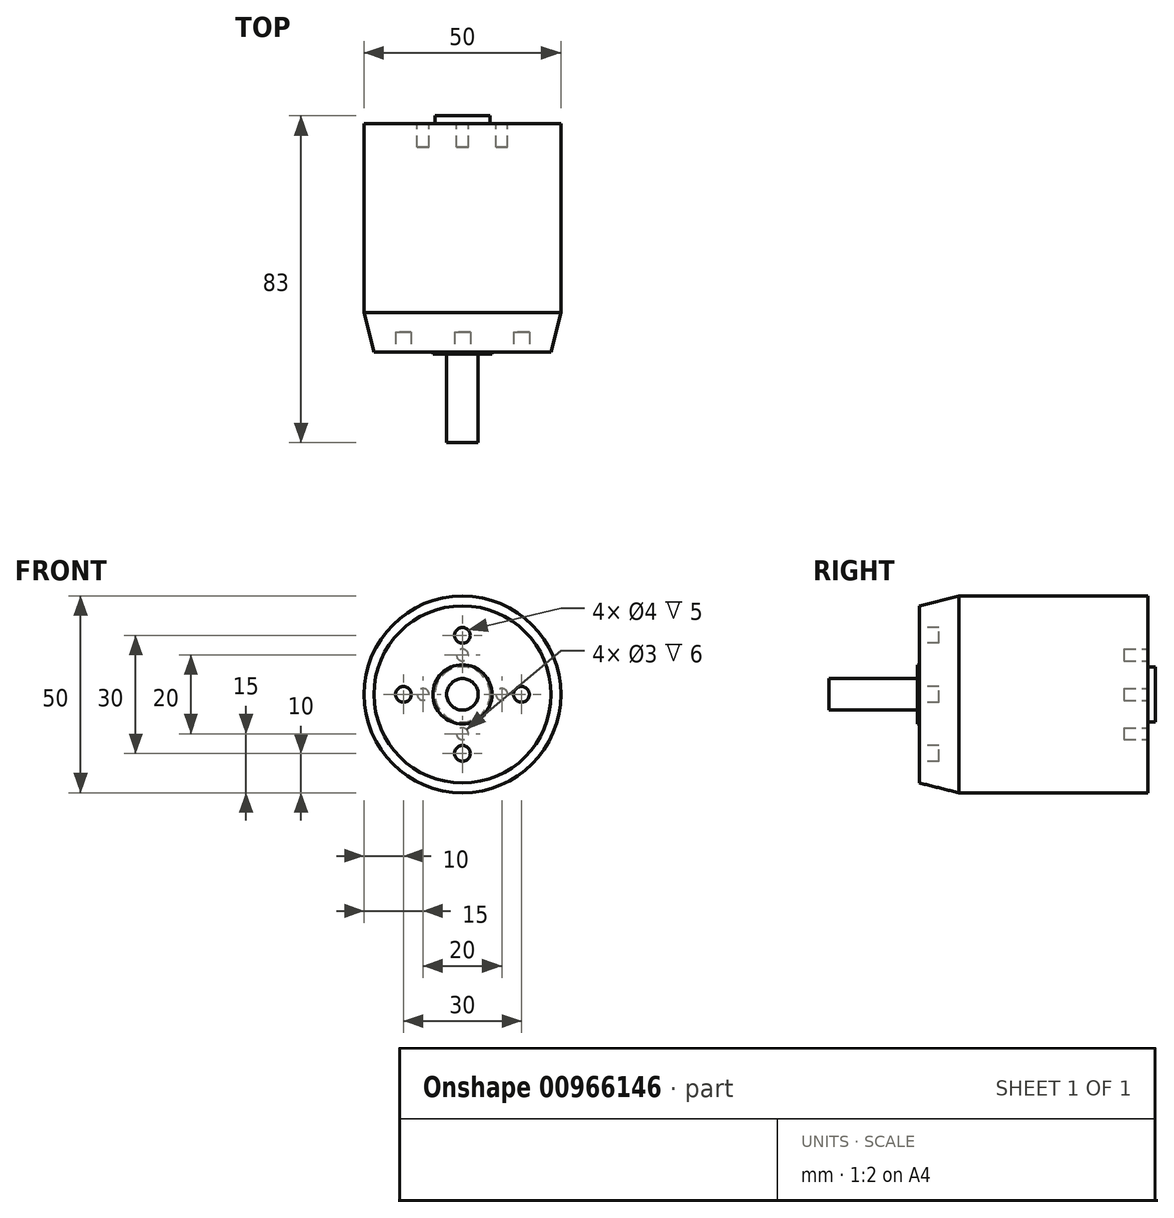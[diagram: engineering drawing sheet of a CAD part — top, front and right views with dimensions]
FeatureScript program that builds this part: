
annotation { "Feature Type Name" : "Feature", "Feature Type Description" : "" }
export const myFeature = defineFeature(function(context is Context, id is Id, definition is map)
    precondition{}
    {
        {
            var Q0;
            Q0=qCreatedBy(makeId("Right.planeOp"),FACE);
            var sketch = newSketch(context, id + "F0", { "sketchPlane" : qUnion([Q0])});
            skLineSegment(sketch, "E0", {"start": v(0, 22.5) * mm, "end": v(0, 4) * mm});
            skLineSegment(sketch, "E1", {"start": v(0, 4) * mm, "end": v(-23, 4) * mm});
            skLineSegment(sketch, "E2", {"start": v(-23, 4) * mm, "end": v(-23, 0) * mm});
            skLineSegment(sketch, "E3", {"start": v(-23, 0) * mm, "end": v(60, 0) * mm});
            skLineSegment(sketch, "E4", {"start": v(0, 22.5) * mm, "end": v(10, 25) * mm});
            skLineSegment(sketch, "E5", {"start": v(10, 25) * mm, "end": v(58, 25) * mm});
            skLineSegment(sketch, "E6", {"start": v(58, 25) * mm, "end": v(58, 7) * mm});
            skLineSegment(sketch, "E7", {"start": v(58, 7) * mm, "end": v(60, 7) * mm});
            skLineSegment(sketch, "E8", {"start": v(60, 7) * mm, "end": v(60, 0) * mm});
            skSolve(sketch);
        }
        {
            var Q0;
            Q0 = qSketchRegion(id + "F0", true);
            var Q1;
            Q1=sQuery(id+"F0.wireOp",EDGE,"E3");
            revolve(context, id + "F1", {"surfaceOperationType" : NewSurfaceOperationType.NEW, "entities" : qUnion([Q0]), "axis" : qUnion([Q1]), "revolveType" : RevolveType.FULL});
        }
        {
            var Q0;
            Q0=makeQuery(id+"F1.opRevolve","SWEPT_FACE",FACE,{"disambiguationData":[OSD([sQuery(id+"F0.wireOp",EDGE,"E0")])]});
            var sketch = newSketch(context, id + "F2", { "sketchPlane" : qUnion([Q0])});
            skCircle(sketch, "E9", {"center": v(15, 0) * mm, "radius": 2 * mm});
            skCircle(sketch, "E10.1.0", {"center": v(0, 15) * mm, "radius": 2 * mm});
            skCircle(sketch, "E10.2.0", {"center": v(-15, 0) * mm, "radius": 2 * mm});
            skCircle(sketch, "E10.3.0", {"center": v(0, -15) * mm, "radius": 2 * mm});
            skPoint(sketch, "E10.center", {"position": v(0, 0) * mm});
            skSolve(sketch);
        }
        {
            var Q0;
            Q0 = qSketchRegion(id + "F2", true);
            extrude(context, id + "F3", {"entities" : qUnion([Q0]), "operationType" : NewBodyOperationType.REMOVE, "oppositeDirection" : true, "depth" : 5 * mm, "offsetDistance" : 25 * mm});
        }
        {
            var Q0;
            Q0=makeQuery(id+"F1.opRevolve","SWEPT_FACE",FACE,{"disambiguationData":[OSD([sQuery(id+"F0.wireOp",EDGE,"E0")])]});
            var sketch = newSketch(context, id + "F4", { "sketchPlane" : qUnion([Q0])});
            skCircle(sketch, "E11", {"center": v(0, 0) * mm, "radius": 7.5 * mm});
            skSolve(sketch);
        }
        {
            var Q0;
            Q0 = qSketchRegion(id + "F4", true);
            extrude(context, id + "F5", {"entities" : qUnion([Q0]), "operationType" : NewBodyOperationType.ADD, "depth" : 0.5 * mm, "offsetDistance" : 25 * mm});
        }
        {
            var Q0;
            Q0=makeQuery(id+"F1.opRevolve","SWEPT_FACE",FACE,{"disambiguationData":[OSD([sQuery(id+"F0.wireOp",EDGE,"E6")])]});
            var sketch = newSketch(context, id + "F6", { "sketchPlane" : qUnion([Q0])});
            skCircle(sketch, "E12", {"center": v(10, 0) * mm, "radius": 1.5 * mm});
            skCircle(sketch, "E13.1.0", {"center": v(0, 10) * mm, "radius": 1.5 * mm});
            skCircle(sketch, "E13.2.0", {"center": v(-10, 0) * mm, "radius": 1.5 * mm});
            skCircle(sketch, "E13.3.0", {"center": v(0, -10) * mm, "radius": 1.5 * mm});
            skPoint(sketch, "E13.center", {"position": v(0, 0) * mm});
            skSolve(sketch);
        }
        {
            var Q0;
            Q0 = qSketchRegion(id + "F6", true);
            extrude(context, id + "F7", {"entities" : qUnion([Q0]), "operationType" : NewBodyOperationType.REMOVE, "oppositeDirection" : true, "depth" : 6 * mm, "offsetDistance" : 25 * mm});
        }
    });
